# Revit family: UNB_Specchio_Multiproduct_BIM_IT_T3354;T3355;T3356;T3357;T3358;T3359;T3360;T3361;T3363;T3594_NEW
name_source: partatom
category: Plumbing Fixtures
revit_build: Autodesk Revit 2017 (Build: 20160225_1515(x64)
units: mm (PartAtom-declared; Revit-internal decimal feet)

## family parameters
Cut with Voids When Loaded = No
Host = Face
Part Type = Normal
Room Calculation Point = No
Round Connector Dimension = Use Diameter
Shared = No

## types (10) — shared parameters
Accessori = http://www.idealstandard.it
Autore = Ideal Standard
Brand = Ideal Standard
CodiceDiPrestazione = EN
Colore = specchio
Connessione = piombatura
Default Elevation = 1500 mm  [stored 4.92126 ft]
DescrizioneClassifcazioneUni2015 = Bathroom furniture
Finitura = specchio
Forma = rettangolare
Garanzia = garanzia del produttore
IfcEsportaCome = BATHROOM FURNITURE
InformazioniDiProdotto = http://www.idealstandard.it
InstruzioniInstallazione = http://www.idealstandard.it
LunghezzaNominale = 26 mm
Materiale = bicchiere
PartiDiRicambio = http://www.idealstandard.it
ProfonditàNominale = 26 mm
Revisione = 1
RiferimentoClassificazioneUni2015 = MIRRORS
Spazio = interno
Telefono = 800 652 290
TipoDiDato = Fisso
TipoEspotazioneIfc = IfcFurnitureType
TipologiaVaso = Altro
URL = http://www.idealstandard.it
UnitàDurata = anno
UnitàDurataGaranzia = anno
UnitàLineare = millimetro
UnitàMonetaria = €
UnitàSuperficie = millimetro
UnitàVolume = litro
Versione = 1
VersioneClassificazioneUni2015 = IfcFurnitureType
zero-valued in all types: Cost, CostoDiSostituzione

## per-type parameters (varying)
| type | AltezzaNominale | Caratteristiche | CodiceABarre | Description | LarghezzaNominale | Model | ModelloDiRiferimento | Nome | NomeOggettoBim | NumeroDiModello | PesoNetto | Riferimento |
| T3354 - 500 x 700 mirror | 700 mm  [stored 2.29659 ft] | SPECCHIO LOW S 50X70 | 8014140447467 | SPECCHIO LOW S 50X70 | 500 mm  [stored 1.64042 ft] | T3354BH | SPECCHIO LOW S 50X70 | ISI_IdealStandard_Specchio_T3354 | ISI_IdealStandard_Specchio_T3354 | T3354BH | 4.59 Kg | T3354 |
| T3355 - 600 x 700 mirror | 700 mm  [stored 2.29659 ft] | SPECCHIO LOW S 60X70 | 8014140447474 | SPECCHIO LOW S 60X70 | 600 mm | T3355BH | SPECCHIO LOW S 60X70 | ISI_IdealStandard_Specchio_T3355 | ISI_IdealStandard_Specchio_T3355 | T3355BH | 5.31 Kg | T3355 |
| T3356 - 700 x 700 mirror | 700 mm  [stored 2.29659 ft] | SPECCHIO LOW S 70X70 | 8014140447481 | SPECCHIO LOW S 70X70 | 700 mm  [stored 2.29659 ft] | T3356BH | SPECCHIO LOW S 70X70 | ISI_IdealStandard_Specchio_T3356 | ISI_IdealStandard_Specchio_T3356 | T3356BH | 6.12 Kg | T3356 |
| T3357 - 800 x 700 mirror | 700 mm  [stored 2.29659 ft] | SPECCHIO LOW S 80X70 | 8014140447498 | SPECCHIO LOW S 80X70 | 800 mm  [stored 2.62467 ft] | T3357BH | SPECCHIO LOW S 80X70 | ISI_IdealStandard_Specchio_T3357 | ISI_IdealStandard_Specchio_T3357 | T3357BH | 6.84 Kg | T3357 |
| T3358 - 1000 x 700 mirror | 700 mm  [stored 2.29659 ft] | SPECCHIO LOW S 100X70 | 8014140447504 | SPECCHIO LOW S 100X70 | 1000 mm  [stored 3.28084 ft] | T3358BH | SPECCHIO LOW S 100X70 | ISI_IdealStandard_Specchio_T3358 | ISI_IdealStandard_Specchio_T3358 | T3358BH | 8.37 Kg | T3358 |
| T3359 - 1200 x 700 mirror | 700 mm  [stored 2.29659 ft] | SPECCHIO LOW S 120X70 | 8014140447511 | SPECCHIO LOW S 120X70 | 1200 mm  [stored 3.93701 ft] | T3359BH | SPECCHIO LOW S 120X70 | ISI_IdealStandard_Specchio_T3359 | ISI_IdealStandard_Specchio_T3359 | T3359BH | 9.45 Kg | T3359 |
| T3360 - 400 x 1000 mirror | 1000 mm  [stored 3.28084 ft] | SPECCHIO LOW H 40X100 | 8014140447528 | SPECCHIO LOW H 40X100 | 400 mm  [stored 1.31234 ft] | T3360BH | SPECCHIO LOW H 40X100 | ISI_IdealStandard_Specchio_T3360 | ISI_IdealStandard_Specchio_T3360 | T3360BH | 5.58 Kg | T3360 |
| T3361 - 600 x 1000 mirror | 1000 mm  [stored 3.28084 ft] | SPECCHIO LOW H 60X100 | 8014140447535 | SPECCHIO LOW H 60X100 | 600 mm | T3361BH | SPECCHIO LOW H 60X100 | ISI_IdealStandard_Specchio_T3361 | ISI_IdealStandard_Specchio_T3361 | T3361BH | 7.02 Kg | T3361 |
| T3363 - 800 x 1000 mirror | 1000 mm  [stored 3.28084 ft] | SPECCHIO LOW H 80X100 | 8014140447559 | SPECCHIO LOW H 80X100 | 800 mm  [stored 2.62467 ft] | T3363BH | SPECCHIO LOW H 80X100 | ISI_IdealStandard_Specchio_T3363 | ISI_IdealStandard_Specchio_T3363 | T3363BH | 8.91 Kg | T3363 |
| T3594 - 1200 x 1000 mirror | 1000 mm  [stored 3.28084 ft] | SPECCHIO LOW H 120X100 | 8014140447993 | SPECCHIO LOW H 120X100 | 1200 mm  [stored 3.93701 ft] | T3594BH | SPECCHIO LOW H 120X100 | ISI_IdealStandard_Specchio_T3594 | ISI_IdealStandard_Specchio_T3594 | T3594BH | 11.16 Kg | T3594 |

note: [stored X ft] marks values corroborated as IEEE doubles in the binary element streams (Revit-internal decimal feet)

## geometry (parser evidence)
native form markers: Sweep x1
no freeform markers — native parametric forms only
